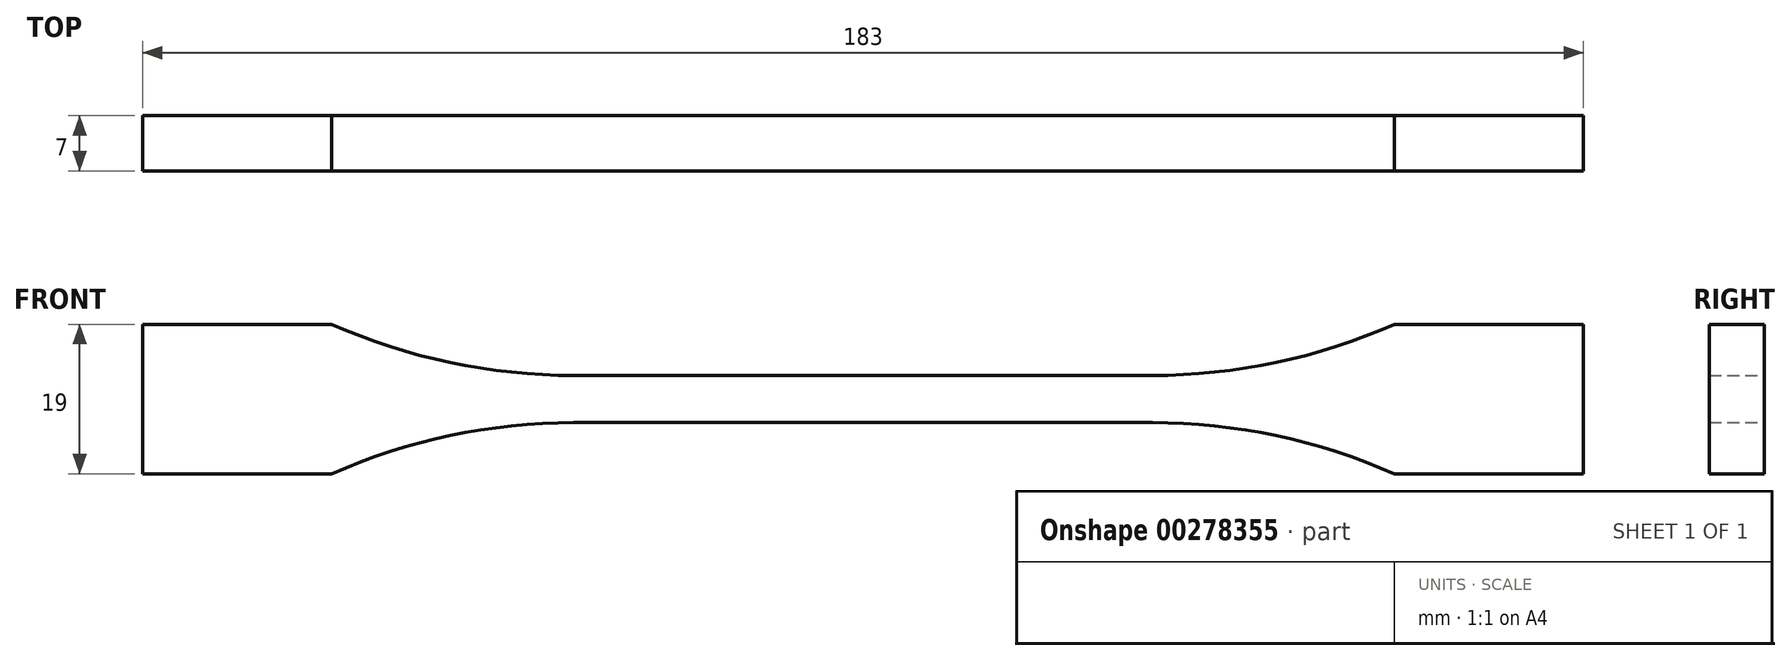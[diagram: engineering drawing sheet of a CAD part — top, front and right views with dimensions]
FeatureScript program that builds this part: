
annotation { "Feature Type Name" : "Feature", "Feature Type Description" : "" }
export const myFeature = defineFeature(function(context is Context, id is Id, definition is map)
    precondition{}
    {
        {
            var Q0;
            Q0=qCreatedBy(makeId("Front.planeOp"),FACE);
            var sketch = newSketch(context, id + "F0", { "sketchPlane" : qUnion([Q0])});
            skLineSegment(sketch, "E0", {"start": v(0, 3) * mm, "end": v(36.75, 3) * mm});
            skArc(sketch, "E1", {"start": v(36.75, 3) * mm, "mid": v(52.46, 4.64) * mm, "end": v(67.5, 9.5) * mm});
            skLineSegment(sketch, "E2", {"start": v(67.5, 9.5) * mm, "end": v(91.5, 9.5) * mm});
            skLineSegment(sketch, "E3.MirrorCS", {"start": v(67.5, -9.5) * mm, "end": v(91.5, -9.5) * mm});
            skLineSegment(sketch, "E4.MirrorCS", {"start": v(0, -3) * mm, "end": v(36.75, -3) * mm});
            skArc(sketch, "E5.MirrorCS", {"start": v(36.75, -3) * mm, "mid": v(52.46, -4.64) * mm, "end": v(67.5, -9.5) * mm});
            skArc(sketch, "E6.MirrorCS", {"start": v(-36.75, -3) * mm, "mid": v(-52.46, -4.64) * mm, "end": v(-67.5, -9.5) * mm});
            skArc(sketch, "E7.MirrorCS", {"start": v(-36.75, 3) * mm, "mid": v(-52.46, 4.64) * mm, "end": v(-67.5, 9.5) * mm});
            skLineSegment(sketch, "E8.MirrorCS", {"start": v(-67.5, -9.5) * mm, "end": v(-91.5, -9.5) * mm});
            skLineSegment(sketch, "E9.MirrorCS", {"start": v(-67.5, 9.5) * mm, "end": v(-91.5, 9.5) * mm});
            skLineSegment(sketch, "E10.MirrorCS", {"start": v(0, -3) * mm, "end": v(-36.75, -3) * mm});
            skLineSegment(sketch, "E11.MirrorCS", {"start": v(0, 3) * mm, "end": v(-36.75, 3) * mm});
            skLineSegment(sketch, "E12", {"start": v(-91.5, -9.5) * mm, "end": v(-91.5, 9.5) * mm});
            skLineSegment(sketch, "E13", {"start": v(91.5, -9.5) * mm, "end": v(91.5, 9.5) * mm});
            skSolve(sketch);
        }
        {
            var Q0;
            Q0=qSketchRegion(id+"F0",true);
            extrude(context, id + "F1", {"entities" : qUnion([Q0]), "endBound" : BoundingType.SYMMETRIC, "depth" : 7 * mm});
        }
    });
